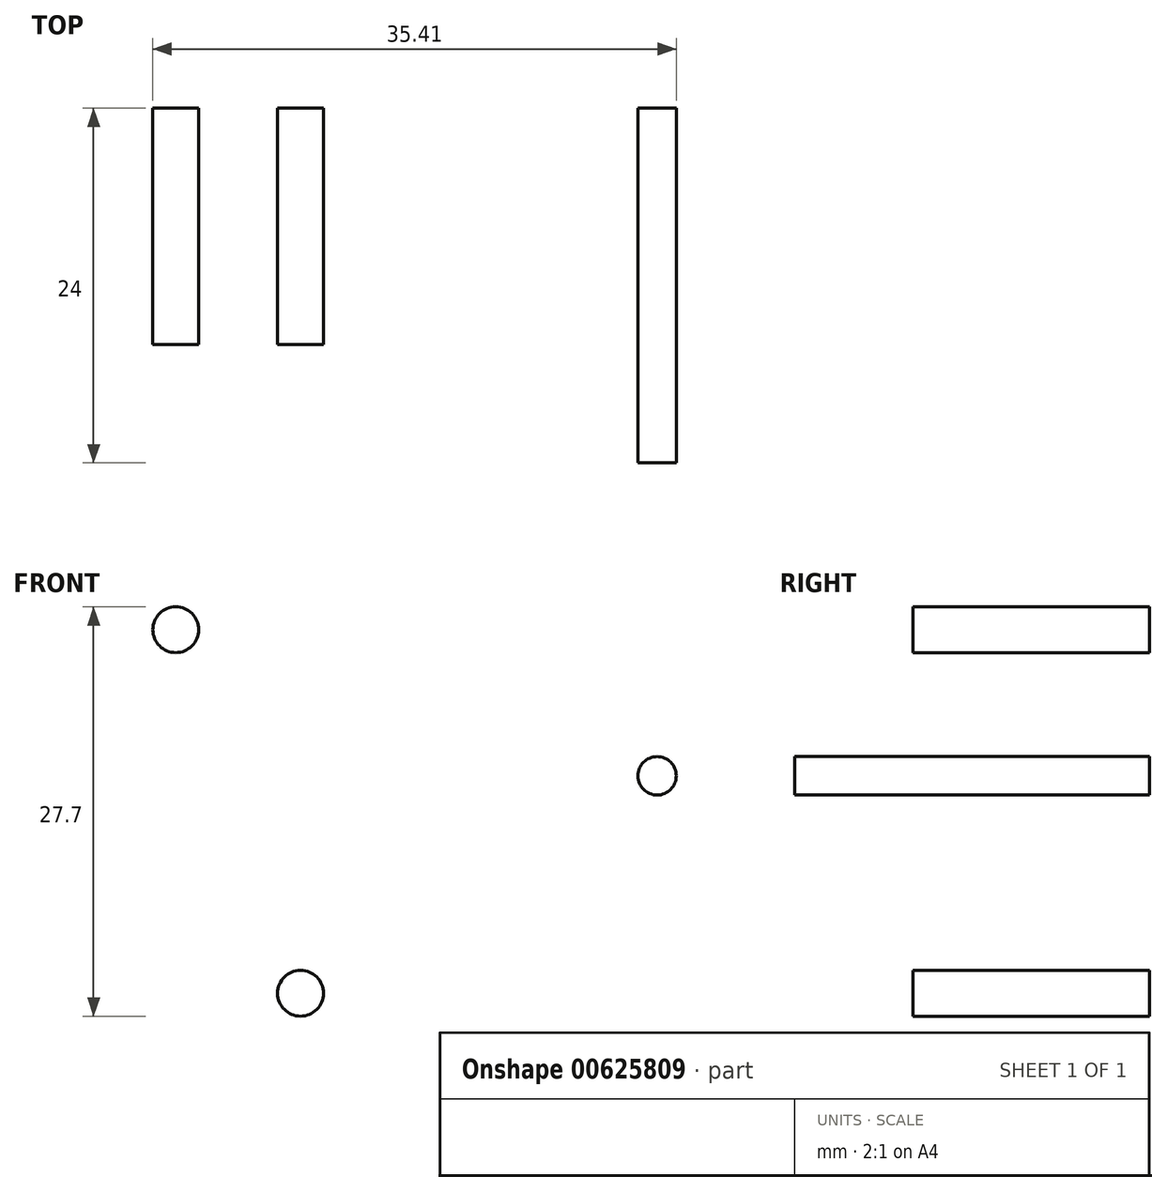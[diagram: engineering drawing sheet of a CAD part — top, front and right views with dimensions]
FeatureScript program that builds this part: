
annotation { "Feature Type Name" : "Feature", "Feature Type Description" : "" }
export const myFeature = defineFeature(function(context is Context, id is Id, definition is map)
    precondition{}
    {
        {
            var Q0;
            Q0=qCreatedBy(makeId("Front.planeOp"),FACE);
            var sketch = newSketch(context, id + "F0", { "sketchPlane" : qUnion([Q0])});
            skCircle(sketch, "E0", {"center": v(-49.08, 32.56) * mm, "radius": 1.55 * mm});
            skSolve(sketch);
        }
        {
            var Q0;
            Q0=makeQuery(id+"F0.imprint","IMPRINT",FACE,{"disambiguationData":[TD([[makeQuery(id+"F0.imprint","IMPRINT",EDGE,{"derivedFrom":sQuery(id+"F0.wireOp",EDGE,"E0")}),1.0]])]});
            extrude(context, id + "F1", {"entities" : qUnion([Q0]), "depth" : 16 * mm, "offsetDistance" : 25 * mm});
        }
        {
            var Q0;
            Q0=qCreatedBy(makeId("Front.planeOp"),FACE);
            var sketch = newSketch(context, id + "F2", { "sketchPlane" : qUnion([Q0])});
            skCircle(sketch, "E1", {"center": v(-40.64, 7.96) * mm, "radius": 1.55 * mm});
            skSolve(sketch);
        }
        {
            var Q0;
            Q0 = qSketchRegion(id + "F2", true);
            extrude(context, id + "F3", {"entities" : qUnion([Q0]), "depth" : 16 * mm, "offsetDistance" : 25 * mm});
        }
        {
            var Q0;
            Q0=qCreatedBy(makeId("Front.planeOp"),FACE);
            var sketch = newSketch(context, id + "F4", { "sketchPlane" : qUnion([Q0])});
            skCircle(sketch, "E2", {"center": v(-16.52, 22.67) * mm, "radius": 1.3 * mm});
            skSolve(sketch);
        }
        {
            var Q0;
            Q0 = qSketchRegion(id + "F4", true);
            extrude(context, id + "F5", {"entities" : qUnion([Q0]), "depth" : 24 * mm, "offsetDistance" : 25 * mm});
        }
    });
